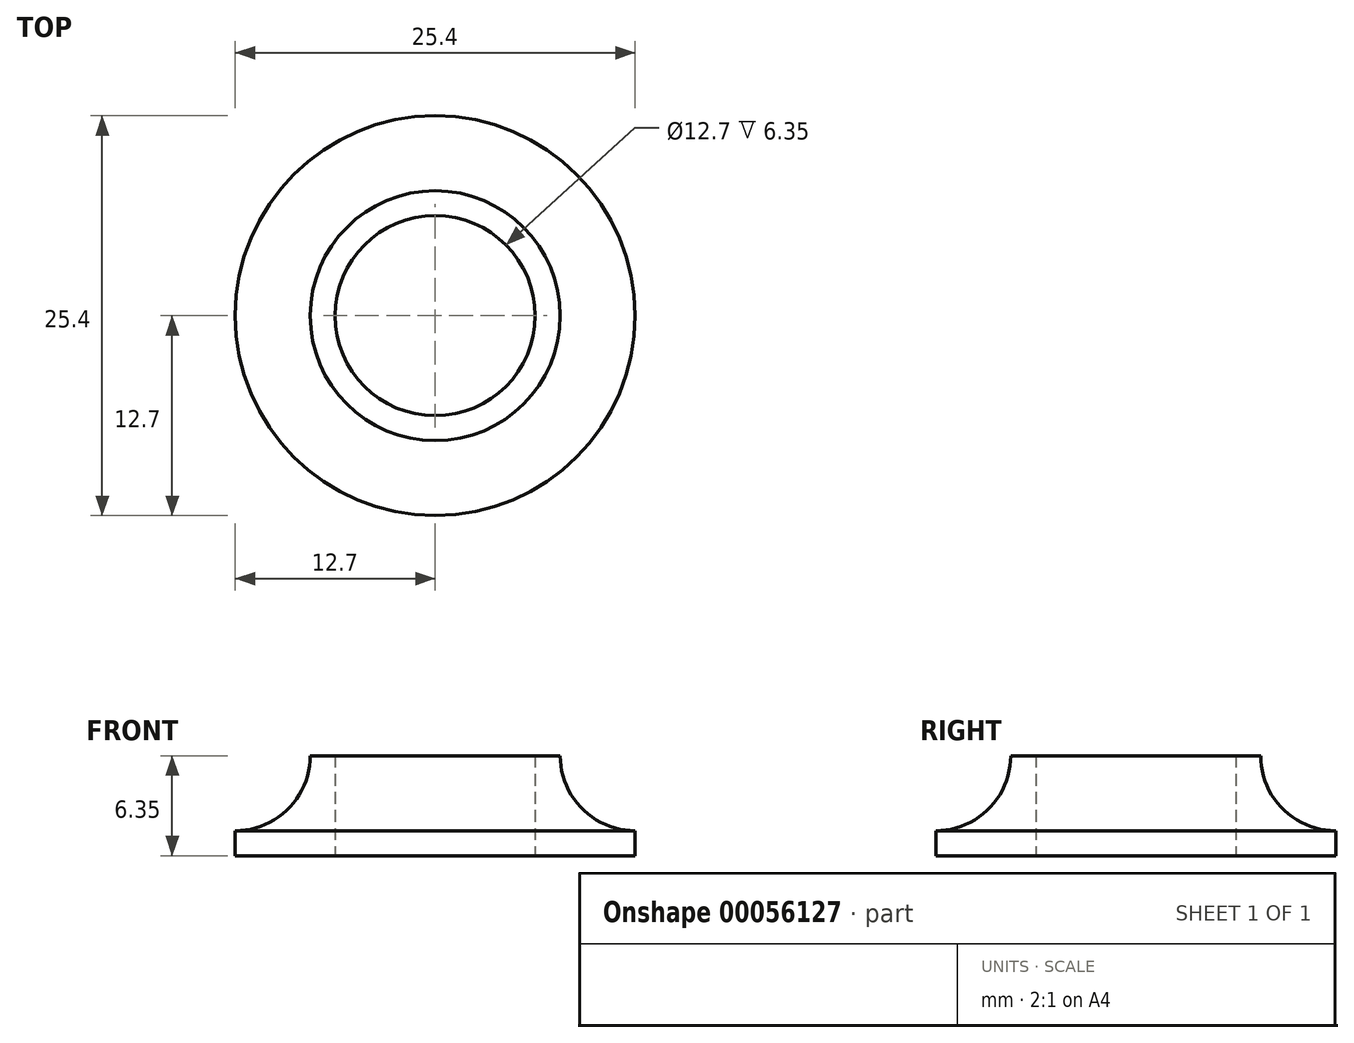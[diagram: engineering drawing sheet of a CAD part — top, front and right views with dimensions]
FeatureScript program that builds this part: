
annotation { "Feature Type Name" : "Feature", "Feature Type Description" : "" }
export const myFeature = defineFeature(function(context is Context, id is Id, definition is map)
    precondition{}
    {
        {
            var Q0;
            Q0=qCreatedBy(makeId("Front.planeOp"),FACE);
            var sketch = newSketch(context, id + "F0", { "sketchPlane" : qUnion([Q0])});
            skLineSegment(sketch, "E0", {"start": v(-7.94, 6.35) * mm, "end": v(-6.35, 6.35) * mm});
            skLineSegment(sketch, "E1", {"start": v(-6.35, 6.35) * mm, "end": v(-6.35, 0) * mm});
            skLineSegment(sketch, "E2", {"start": v(-6.35, 0) * mm, "end": v(-12.7, 0) * mm});
            skLineSegment(sketch, "E3", {"start": v(-12.7, 0) * mm, "end": v(-12.7, 1.59) * mm});
            skArc(sketch, "E4", {"start": v(-12.7, 1.59) * mm, "mid": v(-9.33, 2.98) * mm, "end": v(-7.94, 6.35) * mm});
            skLineSegment(sketch, "E5", {"start": v(0, 0) * mm, "end": v(0, 15.16) * mm, "construction": true});
            skSolve(sketch);
        }
        {
            var Q0;
            Q0=makeQuery(id+"F0.imprint","IMPRINT",FACE,{"disambiguationData":[TD([[makeQuery(id+"F0.imprint","IMPRINT",EDGE,{"derivedFrom":sQuery(id+"F0.wireOp",EDGE,"E0")}),-1.0]])]});
            var Q1;
            Q1=sQuery(id+"F0.wireOp",EDGE,"E5");
            revolve(context, id + "F1", {"entities" : qUnion([Q0]), "axis" : qUnion([Q1]), "revolveType" : RevolveType.FULL});
        }
    });
